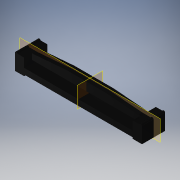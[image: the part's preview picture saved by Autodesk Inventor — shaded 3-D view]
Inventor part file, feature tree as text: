
AUTODESK INVENTOR PART (.ipt)
format: ipt  version: 2019 (Build 230136000, 136)  size: 238,592 bytes
history: native  units: mm (DEFAULTED — no unit token found)
features: sketch x8, extrude x5, fillet x1
ambient origin geometry x8: Origin, YZ Plane, XZ Plane, XY Plane, X Axis, Y Axis, Z Axis, Center Point
bodies: Solid1 (feature_tree)
feature tree (14):
  extrude  "Extrusion1"  Depth=10.0mm
  extrude  "Extrusion2"  Depth=47.0mm
  extrude  "Extrusion3"  Depth=7.4676mm TaperAngle=0.0deg
  extrude  "Extrusion4"  Depth=2.54mm
  extrude  "Extrusion5"  Depth=1.3208mm
  fillet  "Fillet1"  Radius=0.762mm
  sketch  "Sketch8"  dims[d15=8.128mm]
  sketch  "Sketch9"  dims[d16=16.891mm]
  sketch  "Sketch11"  dims[d17=0.508mm d18=3.302mm d19=0.0mm d20=1.143mm d21=3.302mm d22=0.0mm d23=0.5842mm d37=0.508mm d38=0.5842mm d39=0.254mm d40=160.0mm d42=1.27mm d43=10.0mm d45=25.4mm d48=1.27mm d49=1.27mm d50=1.27mm d51=1.27mm d53=1.27mm d54=1.27mm d55=1.27mm d56=1.27mm d57=1.27mm d58=1.27mm d59=1.27mm d60=1.27mm d61=1.27mm d62=1.27mm d64=0.4318mm d65=2.032mm d66=1.27mm d67=0.4318mm d68=0.4318mm d69=1.27mm d70=20.0mm d72=22.86mm d73=10.0mm d75=25.4mm d77=20.0mm d79=1.3843mm d80=10.0mm d82=25.4mm d84=20.0mm d86=1.016mm d87=10.0mm d89=25.4mm d91=20.0mm d93=1.016mm d94=10.0mm d96=25.4mm]
  sketch  "Sketch1"  dims[d0=55.0mm d1=10.0mm]
  sketch  "Sketch2"  dims[d2=7.4676mm d3=0.0mm d4=47.0mm]
  sketch  "Sketch3"  dims[d5=0.5842mm d6=7.4676mm d7=0.0mm]
  sketch  "Sketch4"  dims[d8=47.0mm d9=2.54mm]
  sketch  "Sketch5"  dims[d11=7.4676mm d12=0.0mm d13=1.3208mm d14=0.762mm]
